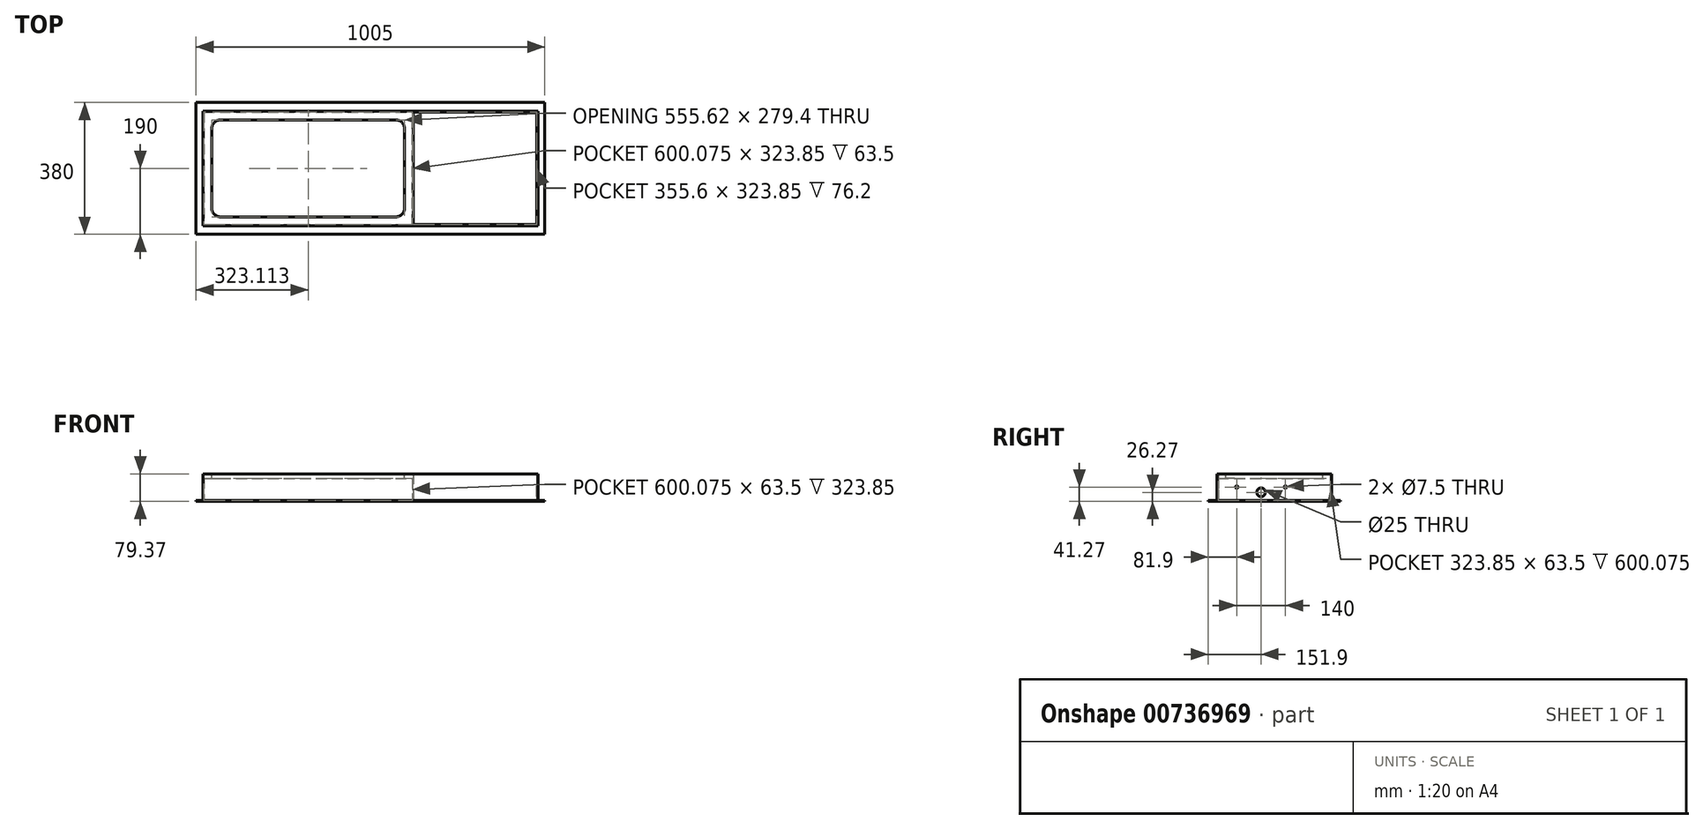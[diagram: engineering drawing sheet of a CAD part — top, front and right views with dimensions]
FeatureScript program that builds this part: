
annotation { "Feature Type Name" : "Feature", "Feature Type Description" : "" }
export const myFeature = defineFeature(function(context is Context, id is Id, definition is map)
    precondition{}
    {
        {
            var Q0;
            Q0=qCreatedBy(makeId("Top.planeOp"),FACE);
            var sketch = newSketch(context, id + "F0", { "sketchPlane" : qUnion([Q0])});
            skLineSegment(sketch, "E0.bottom", {"start": v(502.5, 190) * mm, "end": v(-502.5, 190) * mm});
            skLineSegment(sketch, "E0.top", {"start": v(502.5, -190) * mm, "end": v(-502.5, -190) * mm});
            skLineSegment(sketch, "E0.left", {"start": v(502.5, 190) * mm, "end": v(502.5, -190) * mm});
            skLineSegment(sketch, "E0.right", {"start": v(-502.5, 190) * mm, "end": v(-502.5, -190) * mm});
            skPoint(sketch, "E0.middle", {"position": v(0, 0) * mm});
            skSolve(sketch);
        }
        {
            var Q0;
            Q0=makeQuery(id+"F0.imprint","IMPRINT",FACE,{"disambiguationData":[TD([[makeQuery(id+"F0.imprint","IMPRINT",EDGE,{"derivedFrom":sQuery(id+"F0.wireOp",EDGE,"E0.bottom")}),1.0]])]});
            extrude(context, id + "F1", {"entities" : qUnion([Q0]), "oppositeDirection" : true, "depth" : 3.17 * mm, "offsetDistance" : 25 * mm});
        }
        {
            var Q0;
            Q0=makeQuery(id+"F1.opExtrude","CAP_FACE",FACE,{"disambiguationData":[OSD([sQuery(id+"F0.wireOp",EDGE,"E0.bottom"),sQuery(id+"F0.wireOp",EDGE,"E0.top"),sQuery(id+"F0.wireOp",EDGE,"E0.left"),sQuery(id+"F0.wireOp",EDGE,"E0.right")])],"isStart":true});
            var sketch = newSketch(context, id + "F2", { "sketchPlane" : qUnion([Q0])});
            skLineSegment(sketch, "E1.bottom", {"start": v(482.6, 165.1) * mm, "end": v(-482.6, 165.1) * mm});
            skLineSegment(sketch, "E1.top", {"start": v(482.6, -165.1) * mm, "end": v(-482.6, -165.1) * mm});
            skLineSegment(sketch, "E1.left", {"start": v(482.6, 165.1) * mm, "end": v(482.6, -165.1) * mm});
            skLineSegment(sketch, "E1.right", {"start": v(-482.6, 165.1) * mm, "end": v(-482.6, -165.1) * mm});
            skPoint(sketch, "E1.middle", {"position": v(0, 0) * mm});
            skSolve(sketch);
        }
        {
            var Q0;
            Q0=makeQuery(id+"F2.imprint","IMPRINT",FACE,{"disambiguationData":[TD([[makeQuery(id+"F2.imprint","IMPRINT",EDGE,{"derivedFrom":sQuery(id+"F2.wireOp",EDGE,"E1.bottom")}),1.0]])]});
            extrude(context, id + "F3", {"entities" : qUnion([Q0]), "operationType" : NewBodyOperationType.ADD, "depth" : 76.2 * mm, "offsetDistance" : 25 * mm});
        }
        {
            var Q0;
            Q0=makeQuery(id+"F3.opExtrude","CAP_FACE",FACE,{"disambiguationData":[OSD([sQuery(id+"F2.wireOp",EDGE,"E1.bottom"),sQuery(id+"F2.wireOp",EDGE,"E1.top"),sQuery(id+"F2.wireOp",EDGE,"E1.left"),sQuery(id+"F2.wireOp",EDGE,"E1.right")])],"isStart":false});
            shell(context, id + "F4", {"entities" : qUnion([Q0]), "thickness" : 3.17 * mm});
        }
        {
            var Q0;
            Q0=makeQuery(id+"F3.opExtrude","SWEPT_FACE",FACE,{"disambiguationData":[OSD([sQuery(id+"F2.wireOp",EDGE,"E1.left")])]});
            var sketch = newSketch(context, id + "F5", { "sketchPlane" : qUnion([Q0])});
            skLineSegment(sketch, "E2", {"start": v(-165.1, 38.1) * mm, "end": v(165.1, 38.1) * mm, "construction": true});
            skCircle(sketch, "E3", {"center": v(-38.1, 23.1) * mm, "radius": 12.5 * mm});
            skCircle(sketch, "E4", {"center": v(31.9, 38.1) * mm, "radius": 3.75 * mm});
            skCircle(sketch, "E5", {"center": v(-108.1, 38.1) * mm, "radius": 3.75 * mm});
            skSolve(sketch);
        }
        {
            var Q0;
            Q0=makeQuery(id+"F5.imprint","IMPRINT",FACE,{"disambiguationData":[TD([[makeQuery(id+"F5.imprint","IMPRINT",EDGE,{"derivedFrom":sQuery(id+"F5.wireOp",EDGE,"E5")}),1.0]])]});
            var Q1;
            Q1=makeQuery(id+"F5.imprint","IMPRINT",FACE,{"disambiguationData":[TD([[makeQuery(id+"F5.imprint","IMPRINT",EDGE,{"derivedFrom":sQuery(id+"F5.wireOp",EDGE,"E3")}),1.0]])]});
            var Q2;
            Q2=makeQuery(id+"F5.imprint","IMPRINT",FACE,{"disambiguationData":[TD([[makeQuery(id+"F5.imprint","IMPRINT",EDGE,{"derivedFrom":sQuery(id+"F5.wireOp",EDGE,"E4")}),1.0]])]});
            extrude(context, id + "F6", {"entities" : qUnion([Q0, Q1, Q2]), "operationType" : NewBodyOperationType.REMOVE, "oppositeDirection" : true, "depth" : 3.17 * mm, "offsetDistance" : 25 * mm});
        }
        {
            var Q0;
            Q0=makeQuery(id+"F4.opShell","OFFSET_FACE",FACE,{"disambiguationData":[OSD([sQuery(id+"F0.wireOp",EDGE,"E0.bottom"),sQuery(id+"F0.wireOp",EDGE,"E0.top"),sQuery(id+"F0.wireOp",EDGE,"E0.left"),sQuery(id+"F0.wireOp",EDGE,"E0.right")])]});
            var sketch = newSketch(context, id + "F7", { "sketchPlane" : qUnion([Q0])});
            skLineSegment(sketch, "E6.bottom", {"start": v(123.83, -161.93) * mm, "end": v(120.65, -161.93) * mm});
            skLineSegment(sketch, "E6.top", {"start": v(123.82, 161.93) * mm, "end": v(120.65, 161.93) * mm});
            skLineSegment(sketch, "E6.left", {"start": v(123.83, -161.93) * mm, "end": v(123.82, 161.93) * mm});
            skLineSegment(sketch, "E6.right", {"start": v(120.65, -161.93) * mm, "end": v(120.65, 161.93) * mm});
            skSolve(sketch);
        }
        {
            var Q0;
            Q0=makeQuery(id+"F7.imprint","IMPRINT",FACE,{"disambiguationData":[TD([[makeQuery(id+"F7.imprint","IMPRINT",EDGE,{"derivedFrom":sQuery(id+"F7.wireOp",EDGE,"E6.bottom")}),1.0]])]});
            extrude(context, id + "F8", {"entities" : qUnion([Q0]), "operationType" : NewBodyOperationType.ADD, "depth" : 63.5 * mm, "offsetDistance" : 25 * mm});
        }
        {
            var Q0;
            Q0=makeQuery(id+"F4.opShell","OFFSET_FACE",FACE,{"disambiguationData":[OSD([sQuery(id+"F2.wireOp",EDGE,"E1.top")])]});
            var sketch = newSketch(context, id + "F9", { "sketchPlane" : qUnion([Q0])});
            skLineSegment(sketch, "E7.bottom", {"start": v(-123.83, 63.5) * mm, "end": v(479.43, 63.5) * mm});
            skLineSegment(sketch, "E7.top", {"start": v(-123.83, 76.2) * mm, "end": v(479.43, 76.2) * mm});
            skLineSegment(sketch, "E7.left", {"start": v(-123.83, 63.5) * mm, "end": v(-123.83, 76.2) * mm});
            skLineSegment(sketch, "E7.right", {"start": v(479.43, 63.5) * mm, "end": v(479.43, 76.2) * mm});
            skSolve(sketch);
        }
        {
            var Q0;
            Q0=makeQuery(id+"F9.imprint","IMPRINT",FACE,{"disambiguationData":[TD([[makeQuery(id+"F9.imprint","IMPRINT",EDGE,{"derivedFrom":sQuery(id+"F9.wireOp",EDGE,"E7.top")}),-1.0]])]});
            extrude(context, id + "F10", {"entities" : qUnion([Q0]), "operationType" : NewBodyOperationType.ADD, "depth" : 325 * mm, "offsetDistance" : 25 * mm});
        }
        {
            var Q0;
            Q0=makeQuery(id+"F10.boolean.opBoolean","MERGE",FACE,{"derivedFrom":[makeQuery(id+"F3.opExtrude","CAP_FACE",FACE,{"disambiguationData":[OSD([sQuery(id+"F2.wireOp",EDGE,"E1.bottom"),sQuery(id+"F2.wireOp",EDGE,"E1.top"),sQuery(id+"F2.wireOp",EDGE,"E1.left"),sQuery(id+"F2.wireOp",EDGE,"E1.right")])],"isStart":false}),makeQuery(id+"F10.opExtrude","SWEPT_FACE",FACE,{"disambiguationData":[OSD([sQuery(id+"F9.wireOp",EDGE,"E7.top")])]})]});
            var sketch = newSketch(context, id + "F11", { "sketchPlane" : qUnion([Q0])});
            skLineSegment(sketch, "E8.bottom", {"start": v(-431.8, -139.7) * mm, "end": v(73.03, -139.7) * mm});
            skLineSegment(sketch, "E8.top", {"start": v(-431.8, 139.7) * mm, "end": v(73.03, 139.7) * mm});
            skLineSegment(sketch, "E8.left", {"start": v(-457.2, -114.3) * mm, "end": v(-457.2, 114.3) * mm});
            skLineSegment(sketch, "E8.right", {"start": v(98.43, -114.3) * mm, "end": v(98.42, 114.3) * mm});
            skPoint(sketch, "E8.middle", {"position": v(-179.39, 0) * mm});
            skPoint(sketch, "E9.visualSharp", {"position": v(98.43, -139.7) * mm});
            skArc(sketch, "E9.filletArc", {"start": v(73.03, -139.7) * mm, "mid": v(90.99, -132.26) * mm, "end": v(98.43, -114.3) * mm});
            skPoint(sketch, "E10.visualSharp", {"position": v(-457.2, -139.7) * mm});
            skArc(sketch, "E10.filletArc", {"start": v(-457.2, -114.3) * mm, "mid": v(-449.76, -132.26) * mm, "end": v(-431.8, -139.7) * mm});
            skPoint(sketch, "E11.visualSharp", {"position": v(98.43, 139.7) * mm});
            skArc(sketch, "E11.filletArc", {"start": v(98.42, 114.3) * mm, "mid": v(90.99, 132.26) * mm, "end": v(73.02, 139.7) * mm});
            skPoint(sketch, "E12.visualSharp", {"position": v(-457.2, 139.7) * mm});
            skArc(sketch, "E12.filletArc", {"start": v(-431.8, 139.7) * mm, "mid": v(-449.76, 132.26) * mm, "end": v(-457.2, 114.3) * mm});
            skSolve(sketch);
        }
        {
            var Q0;
            Q0=makeQuery(id+"F11.imprint","IMPRINT",FACE,{"disambiguationData":[TD([[makeQuery(id+"F11.imprint","IMPRINT",EDGE,{"derivedFrom":sQuery(id+"F11.wireOp",EDGE,"E8.bottom")}),1.0]])]});
            extrude(context, id + "F12", {"entities" : qUnion([Q0]), "operationType" : NewBodyOperationType.REMOVE, "oppositeDirection" : true, "depth" : 12.7 * mm, "offsetDistance" : 25 * mm});
        }
    });
